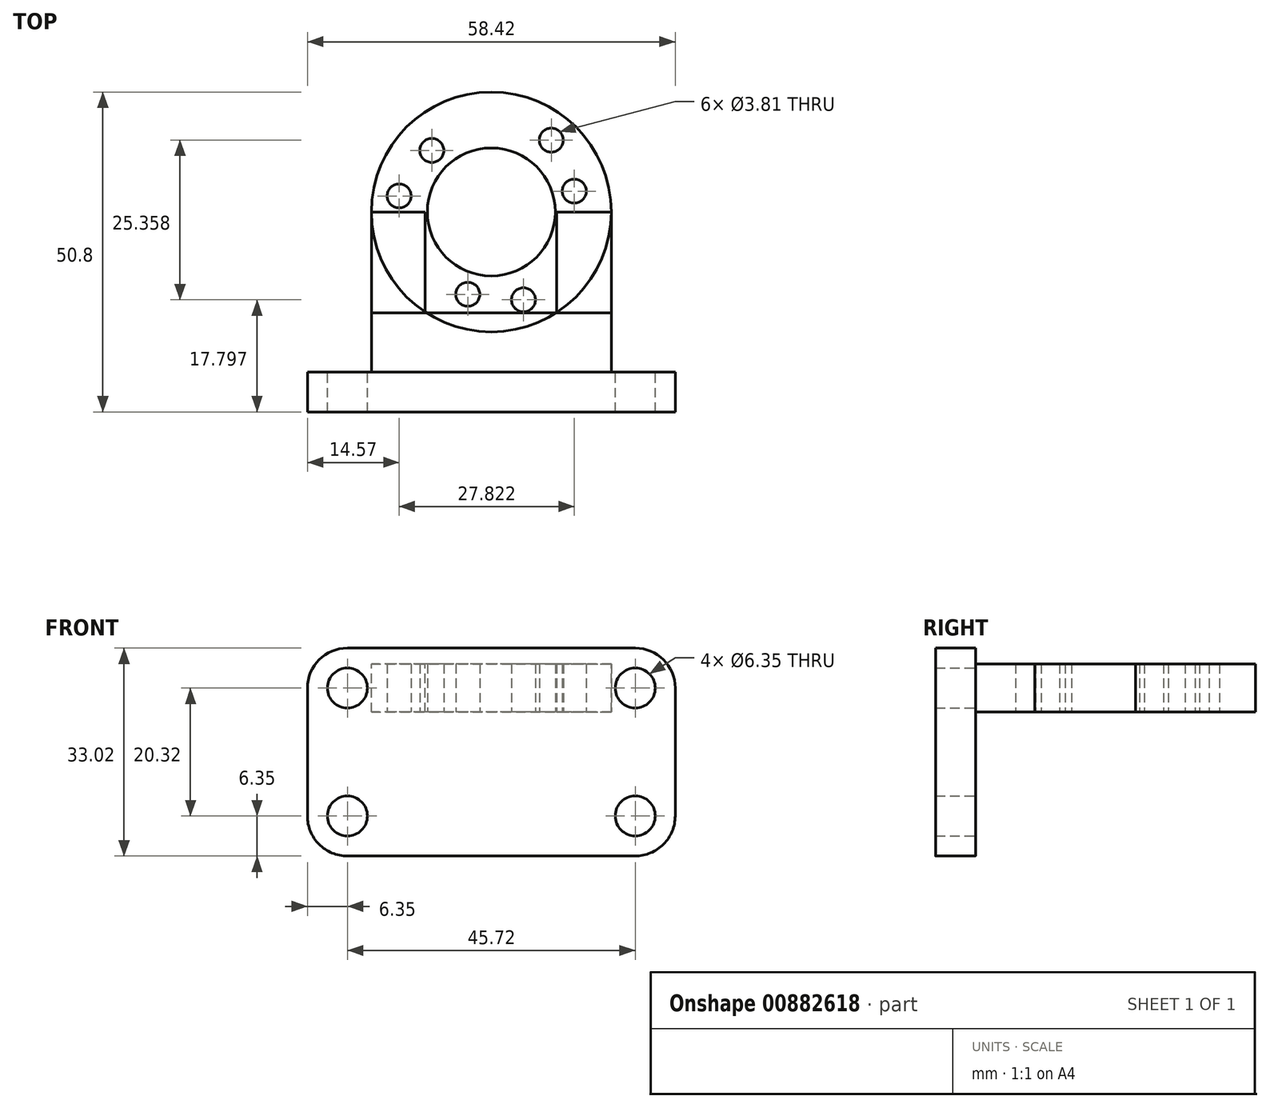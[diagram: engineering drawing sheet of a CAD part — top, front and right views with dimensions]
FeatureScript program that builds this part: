
annotation { "Feature Type Name" : "Feature", "Feature Type Description" : "" }
export const myFeature = defineFeature(function(context is Context, id is Id, definition is map)
    precondition{}
    {
        {
            var Q0;
            Q0=qCreatedBy(makeId("Top.planeOp"),FACE);
            var sketch = newSketch(context, id + "F0", { "sketchPlane" : qUnion([Q0])});
            skCircle(sketch, "E0", {"center": v(0, 25.4) * mm, "radius": 19.05 * mm});
            skCircle(sketch, "E1", {"center": v(0, 25.4) * mm, "radius": 10.16 * mm});
            skCircle(sketch, "E2", {"center": v(-14.64, 27.94) * mm, "radius": 1.9 * mm});
            skCircle(sketch, "E3", {"center": v(-9.45, 35.16) * mm, "radius": 1.9 * mm});
            skCircle(sketch, "E4", {"center": v(9.53, 36.8) * mm, "radius": 1.9 * mm});
            skCircle(sketch, "E5", {"center": v(13.18, 28.7) * mm, "radius": 1.9 * mm});
            skCircle(sketch, "E6", {"center": v(5.1, 11.45) * mm, "radius": 1.9 * mm});
            skCircle(sketch, "E7", {"center": v(-3.74, 12.32) * mm, "radius": 1.9 * mm});
            skSolve(sketch);
        }
        {
            var Q0;
            Q0=makeQuery(id+"F0.imprint","IMPRINT",FACE,{"disambiguationData":[TD([[makeQuery(id+"F0.imprint","IMPRINT",EDGE,{"derivedFrom":sQuery(id+"F0.wireOp",EDGE,"E0")}),1.0]])]});
            extrude(context, id + "F1", {"entities" : qUnion([Q0]), "depth" : 7.62 * mm, "offsetDistance" : 25.4 * mm});
        }
        {
            var Q0;
            Q0=qCreatedBy(makeId("Front.planeOp"),FACE);
            var sketch = newSketch(context, id + "F2", { "sketchPlane" : qUnion([Q0])});
            skCircle(sketch, "E8", {"center": v(-22.86, 3.8) * mm, "radius": 3.18 * mm});
            skCircle(sketch, "E9", {"center": v(22.86, 3.8) * mm, "radius": 3.18 * mm});
            skCircle(sketch, "E10", {"center": v(22.86, -16.5) * mm, "radius": 3.18 * mm});
            skCircle(sketch, "E11", {"center": v(-22.86, -16.51) * mm, "radius": 3.18 * mm});
            skArc(sketch, "E12", {"start": v(29.2, 3.8) * mm, "mid": v(27.35, 8.3) * mm, "end": v(22.86, 10.16) * mm});
            skArc(sketch, "E13", {"start": v(22.86, -22.86) * mm, "mid": v(27.35, -21) * mm, "end": v(29.2, -16.5) * mm});
            skArc(sketch, "E14", {"start": v(-29.2, -16.51) * mm, "mid": v(-27.35, -21) * mm, "end": v(-22.86, -22.86) * mm});
            skArc(sketch, "E15", {"start": v(-22.86, 10.16) * mm, "mid": v(-27.35, 8.3) * mm, "end": v(-29.21, 3.8) * mm});
            skLineSegment(sketch, "E16", {"start": v(22.86, 10.16) * mm, "end": v(-22.86, 10.16) * mm});
            skLineSegment(sketch, "E17", {"start": v(-29.2, 3.8) * mm, "end": v(-29.2, -16.51) * mm});
            skLineSegment(sketch, "E18", {"start": v(-22.86, -22.86) * mm, "end": v(22.86, -22.86) * mm});
            skLineSegment(sketch, "E19", {"start": v(29.2, 3.8) * mm, "end": v(29.2, -16.5) * mm});
            skSolve(sketch);
        }
        {
            var Q0;
            Q0=makeQuery(id+"F2.imprint","IMPRINT",FACE,{"disambiguationData":[TD([[makeQuery(id+"F2.imprint","IMPRINT",EDGE,{"derivedFrom":sQuery(id+"F2.wireOp",EDGE,"gpmNE3Rc-K8zY-xscm-ho3G-kUzZqFBXFjpk.bottom")}),-1.0]])]});
            var Q1;
            Q1=makeQuery(id+"F2.imprint","IMPRINT",FACE,{"disambiguationData":[TD([[makeQuery(id+"F2.imprint","IMPRINT",EDGE,{"derivedFrom":sQuery(id+"F2.wireOp",EDGE,"E8")}),-1.0]])]});
            extrude(context, id + "F3", {"entities" : qUnion([Q0, Q1]), "depth" : 6.35 * mm, "offsetDistance" : 25.4 * mm});
        }
        {
            var Q0;
            Q0=makeQuery(id+"F3.opExtrude","CAP_FACE",FACE,{"disambiguationData":[OSD([sQuery(id+"F2.wireOp",EDGE,"gpmNE3Rc-K8zY-xscm-ho3G-kUzZqFBXFjpk.bottom"),sQuery(id+"F2.wireOp",EDGE,"gpmNE3Rc-K8zY-xscm-ho3G-kUzZqFBXFjpk.top"),sQuery(id+"F2.wireOp",EDGE,"gpmNE3Rc-K8zY-xscm-ho3G-kUzZqFBXFjpk.left"),sQuery(id+"F2.wireOp",EDGE,"gpmNE3Rc-K8zY-xscm-ho3G-kUzZqFBXFjpk.right"),sQuery(id+"F2.wireOp",EDGE,"E8"),sQuery(id+"F2.wireOp",EDGE,"E9"),sQuery(id+"F2.wireOp",EDGE,"E10"),sQuery(id+"F2.wireOp",EDGE,"E11")])],"isStart":true});
            var sketch = newSketch(context, id + "F4", { "sketchPlane" : qUnion([Q0])});
            skLineSegment(sketch, "E20.bottom", {"start": v(19.05, 0) * mm, "end": v(-19.05, 0) * mm});
            skLineSegment(sketch, "E20.top", {"start": v(19.05, 7.62) * mm, "end": v(-19.05, 7.62) * mm});
            skLineSegment(sketch, "E20.left", {"start": v(19.05, 0) * mm, "end": v(19.05, 7.62) * mm});
            skLineSegment(sketch, "E20.right", {"start": v(-19.05, 0) * mm, "end": v(-19.05, 7.62) * mm});
            skSolve(sketch);
        }
        {
            var Q0;
            Q0=makeQuery(id+"F4.imprint","IMPRINT",FACE,{"disambiguationData":[TD([[makeQuery(id+"F4.imprint","IMPRINT",EDGE,{"derivedFrom":sQuery(id+"F4.wireOp",EDGE,"E20.bottom")}),-1.0]])]});
            extrude(context, id + "F5", {"entities" : qUnion([Q0]), "depth" : 9.4 * mm, "offsetDistance" : 25.4 * mm});
        }
        {
            var Q0;
            Q0=makeQuery(id+"F5.opExtrude","CAP_FACE",FACE,{"disambiguationData":[OSD([sQuery(id+"F4.wireOp",EDGE,"E20.bottom"),sQuery(id+"F4.wireOp",EDGE,"E20.top"),sQuery(id+"F4.wireOp",EDGE,"E20.left"),sQuery(id+"F4.wireOp",EDGE,"E20.right")])],"isStart":false});
            var sketch = newSketch(context, id + "F6", { "sketchPlane" : qUnion([Q0])});
            skLineSegment(sketch, "E21.bottom", {"start": v(19.05, 0) * mm, "end": v(10.5, 0) * mm});
            skLineSegment(sketch, "E21.top", {"start": v(19.05, 7.62) * mm, "end": v(10.5, 7.62) * mm});
            skLineSegment(sketch, "E21.left", {"start": v(19.05, 0) * mm, "end": v(19.05, 7.62) * mm});
            skLineSegment(sketch, "E21.right", {"start": v(10.5, 0) * mm, "end": v(10.5, 7.62) * mm});
            skLineSegment(sketch, "E22.bottom", {"start": v(-19.05, 7.62) * mm, "end": v(-10.39, 7.62) * mm});
            skLineSegment(sketch, "E22.top", {"start": v(-19.05, 0) * mm, "end": v(-10.39, 0) * mm});
            skLineSegment(sketch, "E22.left", {"start": v(-19.05, 7.62) * mm, "end": v(-19.05, 0) * mm});
            skLineSegment(sketch, "E22.right", {"start": v(-10.39, 7.62) * mm, "end": v(-10.39, 0) * mm});
            skSolve(sketch);
        }
        {
            var Q0;
            Q0 = qSketchRegion(id + "F6", true);
            extrude(context, id + "F7", {"entities" : qUnion([Q0]), "depth" : 16 * mm, "offsetDistance" : 25.4 * mm});
        }
    });
